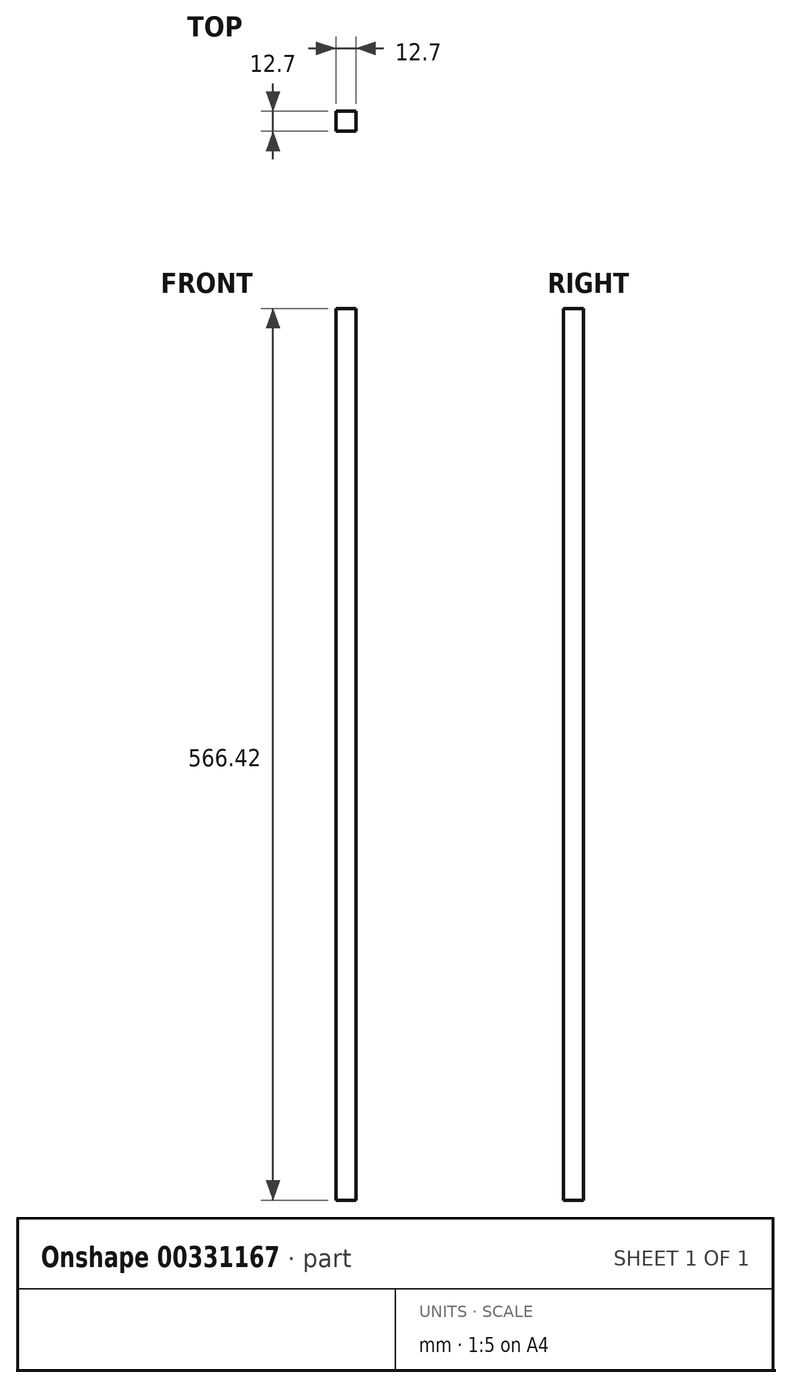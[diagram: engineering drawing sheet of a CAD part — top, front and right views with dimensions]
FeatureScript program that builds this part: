
annotation { "Feature Type Name" : "Feature", "Feature Type Description" : "" }
export const myFeature = defineFeature(function(context is Context, id is Id, definition is map)
    precondition{}
    {
        {
            var Q0;
            Q0=qCreatedBy(makeId("Top.planeOp"),FACE);
            var sketch = newSketch(context, id + "F0", { "sketchPlane" : qUnion([Q0])});
            skLineSegment(sketch, "E0.bottom", {"start": v(6.35, 6.35) * mm, "end": v(-6.35, 6.35) * mm});
            skLineSegment(sketch, "E0.top", {"start": v(6.35, -6.35) * mm, "end": v(-6.35, -6.35) * mm});
            skLineSegment(sketch, "E0.left", {"start": v(6.35, 6.35) * mm, "end": v(6.35, -6.35) * mm});
            skLineSegment(sketch, "E0.right", {"start": v(-6.35, 6.35) * mm, "end": v(-6.35, -6.35) * mm});
            skPoint(sketch, "E0.middle", {"position": v(0, 0) * mm});
            skSolve(sketch);
        }
        {
            var Q0;
            Q0 = qSketchRegion(id + "F0", true);
            extrude(context, id + "F1", {"entities" : qUnion([Q0]), "depth" : 566.42 * mm});
        }
    });
